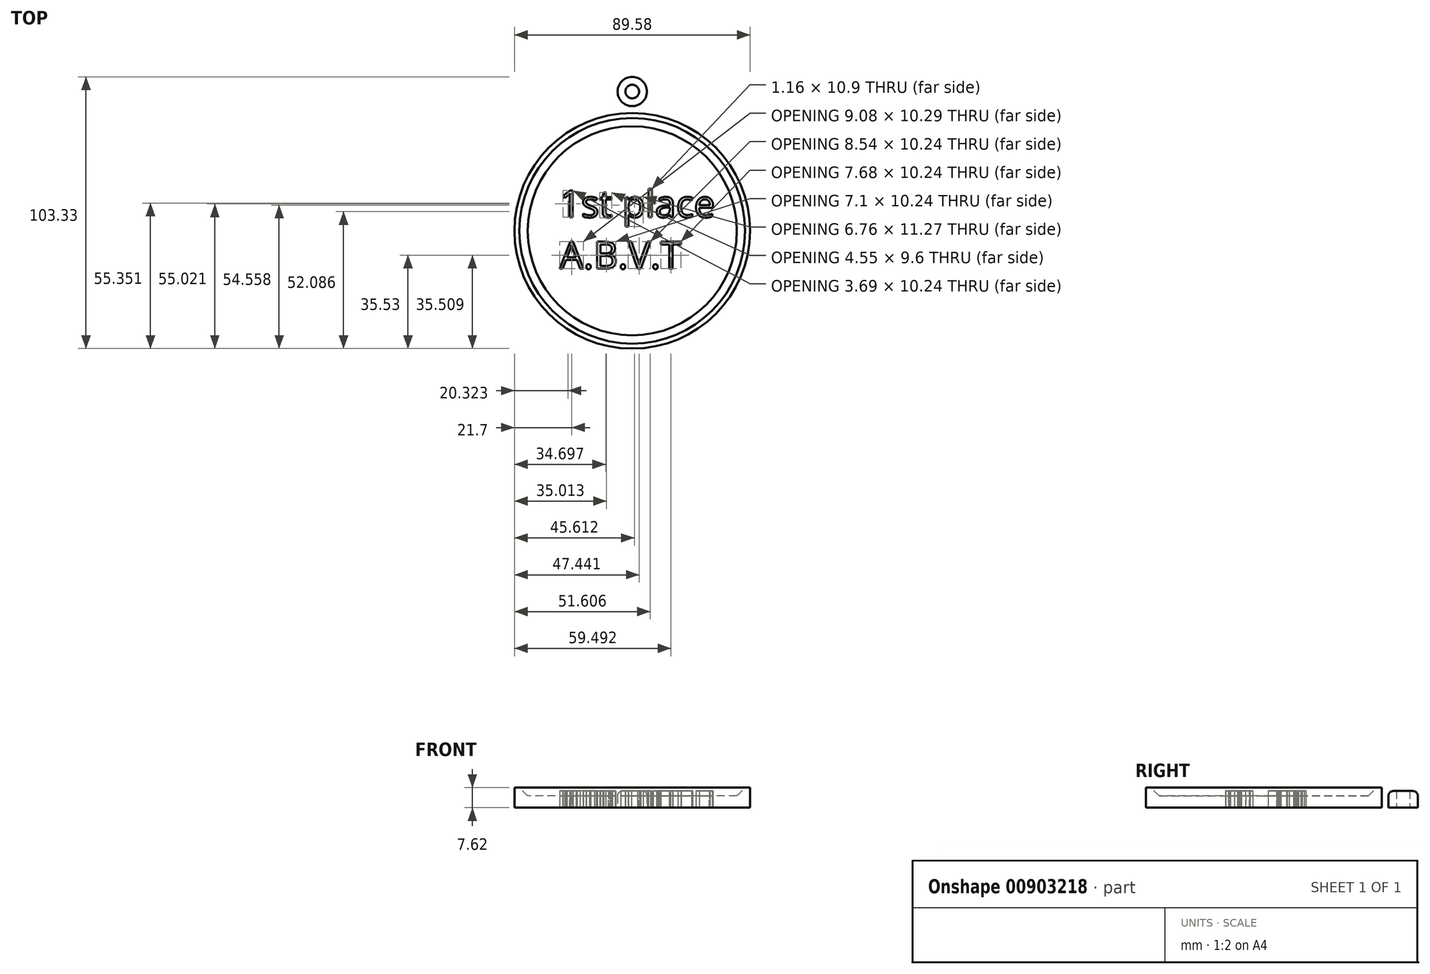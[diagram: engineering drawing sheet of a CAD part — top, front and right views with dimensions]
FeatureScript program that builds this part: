
annotation { "Feature Type Name" : "Feature", "Feature Type Description" : "" }
export const myFeature = defineFeature(function(context is Context, id is Id, definition is map)
    precondition{}
    {
        {
            var Q0;
            Q0=qCreatedBy(makeId("Top.planeOp"),FACE);
            var sketch = newSketch(context, id + "F0", { "sketchPlane" : qUnion([Q0])});
            skText(sketch, "E0", { "text": "1st place\nA.B.V.T", "fontName": "OpenSans-Regular.ttf"});
            skCircle(sketch, "E1", {"center": v(-31.64, -5.11) * mm, "radius": 37.83 * mm});
            skCircle(sketch, "E2", {"center": v(-31.64, -5.11) * mm, "radius": 44.79 * mm});
            skCircle(sketch, "E3", {"center": v(-31.64, 47.86) * mm, "radius": 5.57 * mm});
            skCircle(sketch, "E4", {"center": v(-31.64, 47.86) * mm, "radius": 2.6 * mm});
            const initialGuessF0  = {"E0": [-0.05927, 0, 1, 0, 0.01033]};
            skSetInitialGuess(sketch, initialGuessF0);
            skSolve(sketch);
        }
        {
            var Q0;
            Q0=makeQuery(id+"F0.imprint","IMPRINT",FACE,{"disambiguationData":[TD([[makeQuery(id+"F0.imprint","IMPRINT",EDGE,{"derivedFrom":sQuery(id+"F0.wireOp",EDGE,"E1")}),-1.0]])]});
            extrude(context, id + "F1", {"entities" : qUnion([Q0]), "depth" : 7.62 * mm, "offsetDistance" : 25.4 * mm});
        }
        {
            var Q0;
            Q0=makeQuery(id+"F0.imprint","IMPRINT",FACE,{"disambiguationData":[TD([[makeQuery(id+"F0.imprint","IMPRINT",EDGE,{"derivedFrom":sQuery(id+"F0.wireOp",EDGE,"E3")}),1.0]])]});
            extrude(context, id + "F2", {"entities" : qUnion([Q0]), "depth" : 6.35 * mm, "offsetDistance" : 25.4 * mm});
        }
        {
            var Q0;
            Q0=makeQuery(id+"F2.opExtrude","CAP_EDGE",EDGE,{"disambiguationData":[OSD([sQuery(id+"F0.wireOp",EDGE,"E3")])],"isStart":false});
            fillet(context, id + "F3", {"entities" : qUnion([Q0]), "radius" : 1.84 * mm, "tangentPropagation" : true, "allowEdgeOverflow" : false});
        }
        {
            var Q0;
            Q0=makeQuery(id+"F0.imprint","IMPRINT",FACE,{"disambiguationData":[TD([[makeQuery(id+"F0.imprint","IMPRINT",EDGE,{"derivedFrom":sQuery(id+"F0.wireOp",EDGE,"E0.sketch_text.stroke-0")}),1.0]])]});
            var Q1;
            Q1=makeQuery(id+"F0.imprint","IMPRINT",FACE,{"disambiguationData":[TD([[makeQuery(id+"F0.imprint","IMPRINT",EDGE,{"derivedFrom":sQuery(id+"F0.wireOp",EDGE,"E0.sketch_text.stroke-151")}),1.0]])]});
            var Q2;
            Q2=makeQuery(id+"F0.imprint","IMPRINT",FACE,{"disambiguationData":[TD([[makeQuery(id+"F0.imprint","IMPRINT",EDGE,{"derivedFrom":sQuery(id+"F0.wireOp",EDGE,"E0.sketch_text.stroke-182")}),1.0]])]});
            var Q3;
            Q3=makeQuery(id+"F0.imprint","IMPRINT",FACE,{"disambiguationData":[TD([[makeQuery(id+"F0.imprint","IMPRINT",EDGE,{"derivedFrom":sQuery(id+"F0.wireOp",EDGE,"E0.sketch_text.stroke-175")}),1.0]])]});
            var Q4;
            Q4=makeQuery(id+"F0.imprint","IMPRINT",FACE,{"disambiguationData":[TD([[makeQuery(id+"F0.imprint","IMPRINT",EDGE,{"derivedFrom":sQuery(id+"F0.wireOp",EDGE,"E0.sketch_text.stroke-69")}),1.0]])]});
            var Q5;
            Q5=makeQuery(id+"F0.imprint","IMPRINT",FACE,{"disambiguationData":[TD([[makeQuery(id+"F0.imprint","IMPRINT",EDGE,{"derivedFrom":sQuery(id+"F0.wireOp",EDGE,"E0.sketch_text.stroke-101")}),1.0]])]});
            var Q6;
            Q6=makeQuery(id+"F0.imprint","IMPRINT",FACE,{"disambiguationData":[TD([[makeQuery(id+"F0.imprint","IMPRINT",EDGE,{"derivedFrom":sQuery(id+"F0.wireOp",EDGE,"E0.sketch_text.stroke-138")}),1.0]])]});
            extrude(context, id + "F4", {"entities" : qUnion([Q0, Q1, Q2, Q3, Q4, Q5, Q6]), "operationType" : NewBodyOperationType.ADD, "depth" : 4.44 * mm, "offsetDistance" : 25.4 * mm});
        }
        {
            var Q0;
            Q0=makeQuery(id+"F0.imprint","IMPRINT",FACE,{"disambiguationData":[TD([[makeQuery(id+"F0.imprint","IMPRINT",EDGE,{"derivedFrom":sQuery(id+"F0.wireOp",EDGE,"E0.sketch_text.stroke-0")}),-1.0]])]});
            var Q1;
            Q1=makeQuery(id+"F0.imprint","IMPRINT",FACE,{"disambiguationData":[TD([[makeQuery(id+"F0.imprint","IMPRINT",EDGE,{"derivedFrom":sQuery(id+"F0.wireOp",EDGE,"E0.sketch_text.stroke-9")}),-1.0]])]});
            var Q2;
            Q2=makeQuery(id+"F0.imprint","IMPRINT",FACE,{"disambiguationData":[TD([[makeQuery(id+"F0.imprint","IMPRINT",EDGE,{"derivedFrom":sQuery(id+"F0.wireOp",EDGE,"E0.sketch_text.stroke-34")}),-1.0]])]});
            var Q3;
            Q3=makeQuery(id+"F0.imprint","IMPRINT",FACE,{"disambiguationData":[TD([[makeQuery(id+"F0.imprint","IMPRINT",EDGE,{"derivedFrom":sQuery(id+"F0.wireOp",EDGE,"E0.sketch_text.stroke-53")}),-1.0]])]});
            var Q4;
            Q4=makeQuery(id+"F0.imprint","IMPRINT",FACE,{"disambiguationData":[TD([[makeQuery(id+"F0.imprint","IMPRINT",EDGE,{"derivedFrom":sQuery(id+"F0.wireOp",EDGE,"E0.sketch_text.stroke-78")}),-1.0]])]});
            var Q5;
            Q5=makeQuery(id+"F0.imprint","IMPRINT",FACE,{"disambiguationData":[TD([[makeQuery(id+"F0.imprint","IMPRINT",EDGE,{"derivedFrom":sQuery(id+"F0.wireOp",EDGE,"E0.sketch_text.stroke-82")}),-1.0]])]});
            var Q6;
            Q6=makeQuery(id+"F0.imprint","IMPRINT",FACE,{"disambiguationData":[TD([[makeQuery(id+"F0.imprint","IMPRINT",EDGE,{"derivedFrom":sQuery(id+"F0.wireOp",EDGE,"E0.sketch_text.stroke-109")}),-1.0]])]});
            var Q7;
            Q7=makeQuery(id+"F0.imprint","IMPRINT",FACE,{"disambiguationData":[TD([[makeQuery(id+"F0.imprint","IMPRINT",EDGE,{"derivedFrom":sQuery(id+"F0.wireOp",EDGE,"E0.sketch_text.stroke-124")}),-1.0]])]});
            var Q8;
            Q8=makeQuery(id+"F0.imprint","IMPRINT",FACE,{"disambiguationData":[TD([[makeQuery(id+"F0.imprint","IMPRINT",EDGE,{"derivedFrom":sQuery(id+"F0.wireOp",EDGE,"E0.sketch_text.stroke-143")}),-1.0]])]});
            var Q9;
            Q9=makeQuery(id+"F0.imprint","IMPRINT",FACE,{"disambiguationData":[TD([[makeQuery(id+"F0.imprint","IMPRINT",EDGE,{"derivedFrom":sQuery(id+"F0.wireOp",EDGE,"E0.sketch_text.stroke-156")}),-1.0]])]});
            var Q10;
            Q10=makeQuery(id+"F0.imprint","IMPRINT",FACE,{"disambiguationData":[TD([[makeQuery(id+"F0.imprint","IMPRINT",EDGE,{"derivedFrom":sQuery(id+"F0.wireOp",EDGE,"E0.sketch_text.stroke-164")}),-1.0]])]});
            var Q11;
            Q11=makeQuery(id+"F0.imprint","IMPRINT",FACE,{"disambiguationData":[TD([[makeQuery(id+"F0.imprint","IMPRINT",EDGE,{"derivedFrom":sQuery(id+"F0.wireOp",EDGE,"E0.sketch_text.stroke-189")}),-1.0]])]});
            var Q12;
            Q12=makeQuery(id+"F0.imprint","IMPRINT",FACE,{"disambiguationData":[TD([[makeQuery(id+"F0.imprint","IMPRINT",EDGE,{"derivedFrom":sQuery(id+"F0.wireOp",EDGE,"E0.sketch_text.stroke-197")}),-1.0]])]});
            var Q13;
            Q13=makeQuery(id+"F0.imprint","IMPRINT",FACE,{"disambiguationData":[TD([[makeQuery(id+"F0.imprint","IMPRINT",EDGE,{"derivedFrom":sQuery(id+"F0.wireOp",EDGE,"E0.sketch_text.stroke-206")}),-1.0]])]});
            var Q14;
            Q14=makeQuery(id+"F0.imprint","IMPRINT",FACE,{"disambiguationData":[TD([[makeQuery(id+"F0.imprint","IMPRINT",EDGE,{"derivedFrom":sQuery(id+"F0.wireOp",EDGE,"E0.sketch_text.stroke-214")}),-1.0]])]});
            extrude(context, id + "F5", {"entities" : qUnion([Q0, Q1, Q2, Q3, Q4, Q5, Q6, Q7, Q8, Q9, Q10, Q11, Q12, Q13, Q14]), "depth" : 6.35 * mm, "offsetDistance" : 25.4 * mm});
        }
        {
            var Q0;
            Q0=makeQuery(id+"F1.opExtrude","CAP_EDGE",EDGE,{"disambiguationData":[OSD([sQuery(id+"F0.wireOp",EDGE,"E1")])],"isStart":false});
            chamfer(context, id + "F6", {"entities" : qUnion([Q0]), "width" : 5.08 * mm, "tangentPropagation" : true});
        }
    });
